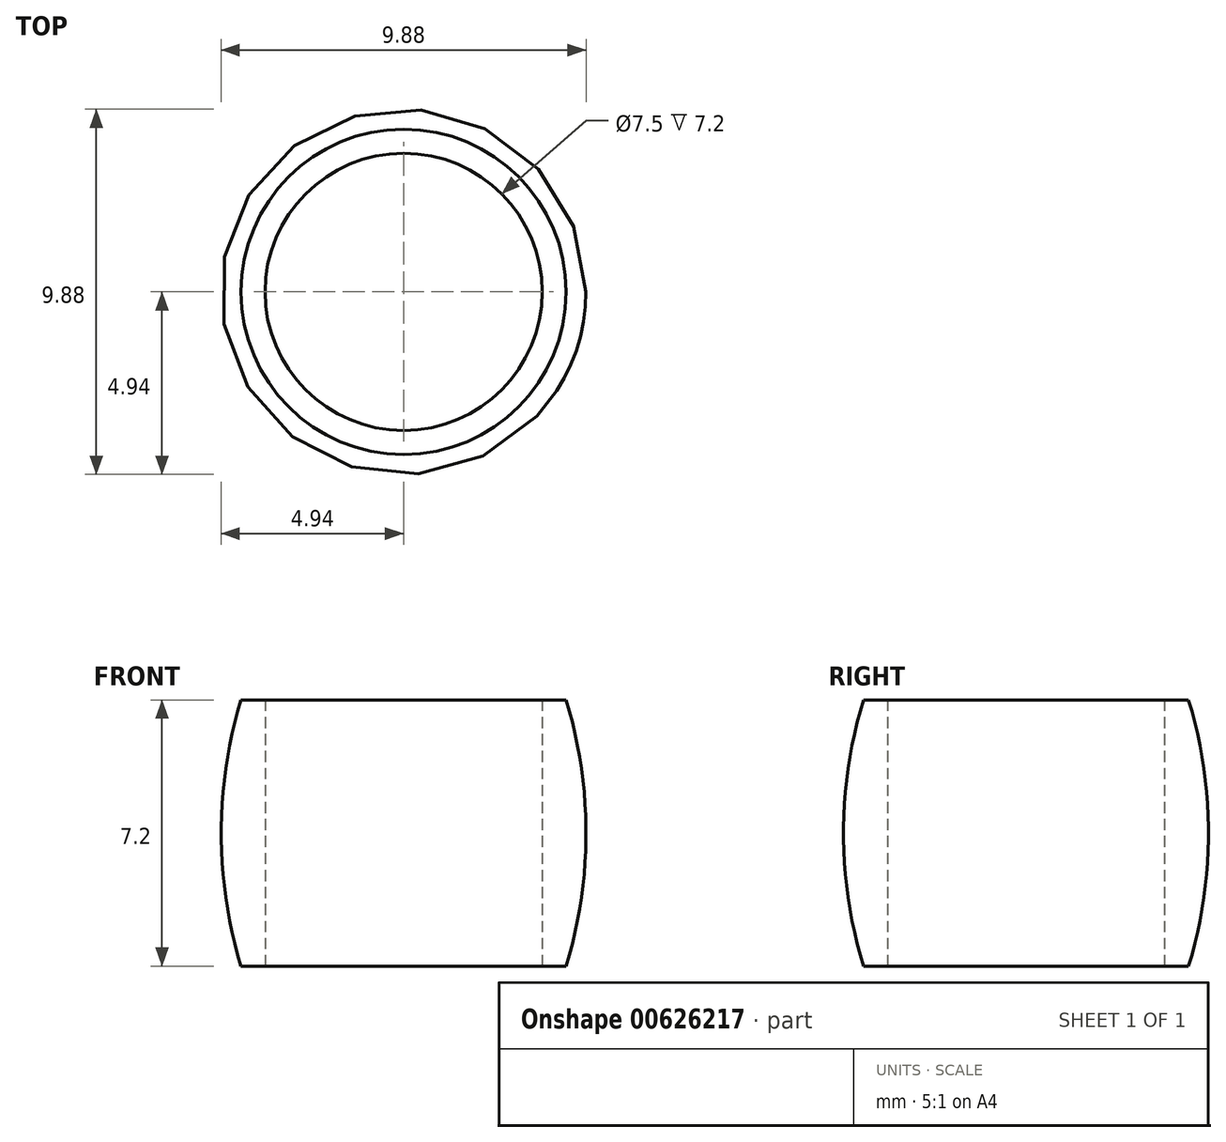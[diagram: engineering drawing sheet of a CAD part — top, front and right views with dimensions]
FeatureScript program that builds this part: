
annotation { "Feature Type Name" : "Feature", "Feature Type Description" : "" }
export const myFeature = defineFeature(function(context is Context, id is Id, definition is map)
    precondition{}
    {
        {
            var Q0;
            Q0=qCreatedBy(makeId("Top.planeOp"),FACE);
            var sketch = newSketch(context, id + "F0", { "sketchPlane" : qUnion([Q0])});
            skCircle(sketch, "E0", {"center": v(0, 0) * mm, "radius": 3.75 * mm});
            skCircle(sketch, "E1", {"center": v(0, 0) * mm, "radius": 4.4 * mm});
            skSolve(sketch);
        }
        {
            var Q0;
            Q0=makeQuery(id+"F0.imprint","IMPRINT",FACE,{"disambiguationData":[TD([[makeQuery(id+"F0.imprint","IMPRINT",EDGE,{"derivedFrom":sQuery(id+"F0.wireOp",EDGE,"E0")}),-1.0]])]});
            extrude(context, id + "F1", {"entities" : qUnion([Q0]), "depth" : 7.2 * mm, "offsetDistance" : 25 * mm});
        }
        {
            var Q0;
            Q0=qCreatedBy(makeId("Front.planeOp"),FACE);
            var sketch = newSketch(context, id + "F2", { "sketchPlane" : qUnion([Q0])});
            skLineSegment(sketch, "E2.0", {"start": v(-4.4, 7.2) * mm, "end": v(4.4, 7.2) * mm});
            skLineSegment(sketch, "E2.1", {"start": v(-4.4, 0) * mm, "end": v(4.4, 0) * mm});
            skArc(sketch, "E3", {"start": v(4.4, 0) * mm, "mid": v(4.94, 3.6) * mm, "end": v(4.4, 7.2) * mm});
            skLineSegment(sketch, "E4", {"start": v(4.4, 7.2) * mm, "end": v(4.4, 0) * mm});
            skLineSegment(sketch, "E5", {"start": v(0, 0) * mm, "end": v(0, 7.2) * mm, "construction": true});
            skSolve(sketch);
        }
        {
            var Q0;
            Q0=makeQuery(id+"F2.imprint","IMPRINT",FACE,{"disambiguationData":[TD([[makeQuery(id+"F2.imprint","IMPRINT",EDGE,{"derivedFrom":sQuery(id+"F2.wireOp",EDGE,"E3")}),1.0]])]});
            var Q1;
            Q1=sQuery(id+"F2.wireOp",EDGE,"E5");
            revolve(context, id + "F3", {"operationType" : NewBodyOperationType.ADD, "entities" : qUnion([Q0]), "axis" : qUnion([Q1]), "revolveType" : RevolveType.FULL});
        }
    });
